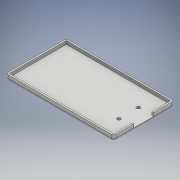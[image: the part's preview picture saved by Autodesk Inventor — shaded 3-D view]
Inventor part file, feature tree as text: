
AUTODESK INVENTOR PART (.ipt)
format: ipt  version: 2018.3 (Build 223284000, 284)  size: 164,864 bytes
history: native  units: mm
features: extrude x4, sketch x4, fillet x2, chamfer x1
ambient origin geometry x8: Origin, YZ Plane, XZ Plane, XY Plane, X Axis, Y Axis, Z Axis, Center Point
bodies: Solid1 (feature_tree)
feature tree (11):
  extrude  "Extrusion1"  Depth=35.56mm
  extrude  "Extrusion2"  Depth=2.0mm TaperAngle=0.0deg
  fillet  "Fillet1"  Radius=1.0mm
  fillet  "Fillet2"  Radius=1.5mm
  extrude  "Extrusion3"  Depth=2.0mm
  chamfer  "Chamfer1"  Distance=12.0mm
  extrude  "Extrusion4"  Depth=1.0mm TaperAngle=0.0deg
  sketch  "Sketch1"  dims[d0=63.5mm d1=35.56mm]
  sketch  "Sketch2"  dims[d2=0.9mm d3=2.0mm d4=0.0mm d5=1.0mm d6=0.0mm d7=1.5mm]
  sketch  "Sketch3"  dims[d8=0.4mm d9=2.0mm]
  sketch  "Sketch4"  dims[d10=12.0mm d11=12.0mm d12=1.0mm d13=0.0mm d14=0.5mm d15=1.0mm d16=45.0deg d17=2.0mm d18=12.0mm d19=9.0mm d20=2.0mm d21=0.0mm d22=2.0mm d23=12.0mm]
